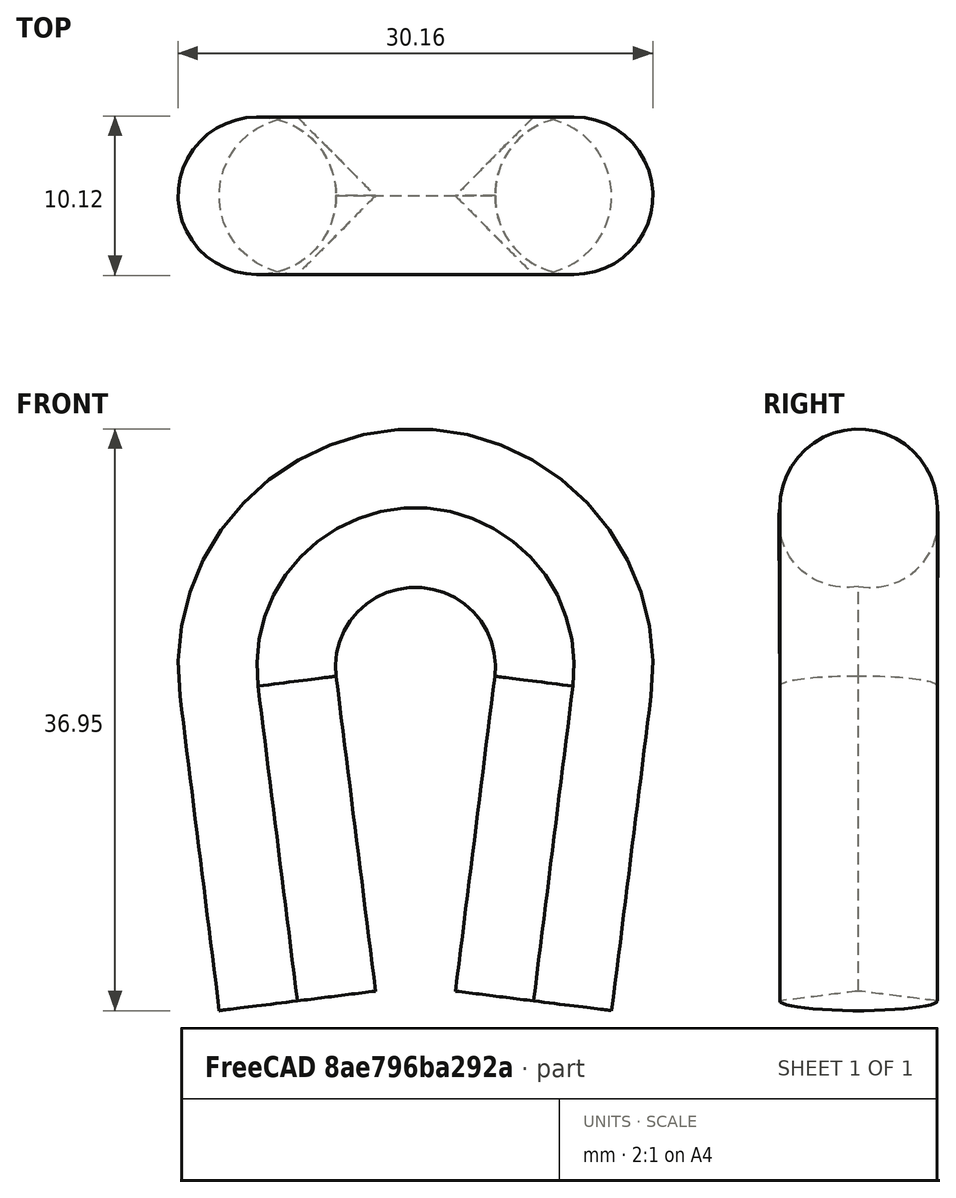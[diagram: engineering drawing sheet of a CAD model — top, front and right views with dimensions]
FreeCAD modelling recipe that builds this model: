
FCSTD DOCUMENT  (FreeCAD 0.18.4R)
Label: SweepTest
License: All rights reserved
LicenseURL: http://en.wikipedia.org/wiki/All_rights_reserved
objects: Sketcher::SketchObject×4, PartDesign::Plane×3, PartDesign::AdditivePipe×1, PartDesign::Body×1
note: 10 computed .brp shape members not serialized (recipe doc carries the construction recipe); baked Part::Feature solids carry a one-line shape summary decoded from their .brp

FEATURE [Sketcher::SketchObject] Sketch001
  MapMode = 5
  Placement = pos=(0,0,0) rot=(1,0,0;1.5708rad)
  Support = -> [XZ_Plane]
  sketch-geometry (4):
    g0: LineSegment StartX=-7.5 StartY=0 StartZ=0 EndX=-10 EndY=20 EndZ=0
    g1: LineSegment StartX=7.5 StartY=0 StartZ=0 EndX=10 EndY=20 EndZ=0
    g2: LineSegment [constr] StartX=-10 StartY=20 StartZ=0 EndX=10 EndY=20 EndZ=0
    g3: ArcOfCircle CenterX=0 CenterY=21.25 CenterZ=0 NormalX=0 NormalY=0 NormalZ=1 AngleXU=0 Radius=10.0778 StartAngle=6.15883 EndAngle=9.54913
  constraints (12):
    c: PointOnObject(g0,g-1)
    c: PointOnObject(g1,g-1)
    c: Coincident(g2,g0)
    c: Coincident(g2,g1)
    c: Horizontal(g2)
    c: Equal(g0,g1)
    c: Tangent(g3,g0) = 1.5708
    c: DistanceX(g0,g1) = 15
    c: DistanceX(g2,g2) = 20
    c: Tangent(g3,g1) = -1.5708
    c: PointOnObject(g3,g-2)
    c: DistanceY(g1,g1) = 20
FEATURE [PartDesign::Plane] DatumPlane
  Length = 25.6765
  MapMode = 7
  Placement = pos=(-7.5,0,1e-16) rot=(0.706423,0.706423,0.04398;3.05369rad)
  ResizeMode = 0
  Support = -> [Sketch001]
  Width = 45.9554
FEATURE [Sketcher::SketchObject] Sketch
  MapMode = 5
  Placement = pos=(-7.5,0,2e-16) rot=(0.706423,0.706423,0.04398;3.05369rad)
  Support = -> [DatumPlane]
  sketch-geometry (5):
    g0: ArcOfCircle CenterX=0 CenterY=0 CenterZ=0 NormalX=0 NormalY=0 NormalZ=1 AngleXU=0 Radius=5 StartAngle=3.14159 EndAngle=6.28319
    g1: ArcOfCircle [constr] CenterX=0 CenterY=0 CenterZ=0 NormalX=0 NormalY=0 NormalZ=1 AngleXU=0 Radius=5 StartAngle=0 EndAngle=3.14159
    g2: LineSegment [constr] StartX=5 StartY=-8.3e-15 StartZ=0 EndX=-5 EndY=-8.3e-15 EndZ=0
    g3: LineSegment StartX=5 StartY=-8.3e-15 StartZ=0 EndX=9e-16 EndY=5 EndZ=0
    g4: LineSegment StartX=9e-16 StartY=5 StartZ=0 EndX=-5 EndY=-8e-15 EndZ=0
  constraints (14):
    c: Coincident(g1,g0)
    c: Coincident(g1,g0)
    c: Coincident(g1,g0)
    c: Radius(g0) = 5
    c: Coincident(g2,g0)
    c: Coincident(g2,g0)
    c: Coincident(g3,g0)
    c: Coincident(g4,g3)
    c: Coincident(g4,g0)
    c: Equal(g3,g4)
    c: PointOnObject(g0,g2)
    c: Coincident(g0,g-1)
    c: PointOnObject(g3,g1)
    c: Horizontal(g2)
FEATURE [PartDesign::Plane] DatumPlane001
  Length = 25.6765
  MapMode = 1
  Placement = pos=(-10,4.4e-15,20) rot=(0.706423,0.706423,0.04398;3.05369rad)
  ResizeMode = 0
  Support = -> [Sketch001]
  Width = 45.9554
FEATURE [Sketcher::SketchObject] Sketch002
  MapMode = 5
  Placement = pos=(-10,4.4e-15,20) rot=(0.706423,0.706423,0.04398;3.05369rad)
  Support = -> [DatumPlane001]
  sketch-geometry (1):
    g0: Circle CenterX=0 CenterY=0 CenterZ=0 NormalX=0 NormalY=0 NormalZ=1 AngleXU=0 Radius=5
  constraints (2):
    c: Coincident(g0,g-1)
    c: Radius(g0) = 5
FEATURE [PartDesign::Plane] DatumPlane002
  Length = 25.6765
  MapMode = 1
  Placement = pos=(10,4.4e-15,20) rot=(0.706423,-0.706423,-0.04398;3.05369rad)
  ResizeMode = 0
  Support = -> [Sketch001]
  Width = 45.9554
FEATURE [Sketcher::SketchObject] Sketch003
  MapMode = 5
  Placement = pos=(10,4.4e-15,20) rot=(0.706423,-0.706423,-0.04398;3.05369rad)
  Support = -> [DatumPlane002]
  sketch-geometry (1):
    g0: Circle CenterX=0 CenterY=0 CenterZ=0 NormalX=0 NormalY=0 NormalZ=1 AngleXU=0 Radius=5
  constraints (2):
    c: Coincident(g0,g-1)
    c: Radius(g0) = 5
FEATURE [PartDesign::AdditivePipe] AdditivePipe
  AuxilleryCurvelinear = true
  AuxillerySpineTangent = false
  Binormal = (0,0,0)
  Mode = 2
  Placement = pos=(-7.5,0,1e-16) rot=(0.706423,0.706423,0.04398;3.05369rad)
  Profile = -> Sketch
  Sections = -> [Sketch002,Sketch003]
  Spine = -> Sketch001
  SpineTangent = false
  Transformation = 1
  Transition = 0
FEATURE [PartDesign::Body] Body
  Group = -> [Sketch,Sketch001,DatumPlane,AdditivePipe,DatumPlane001,Sketch002,DatumPlane002,Sketch003]
  Origin = -> Origin
  Tip = -> AdditivePipe
